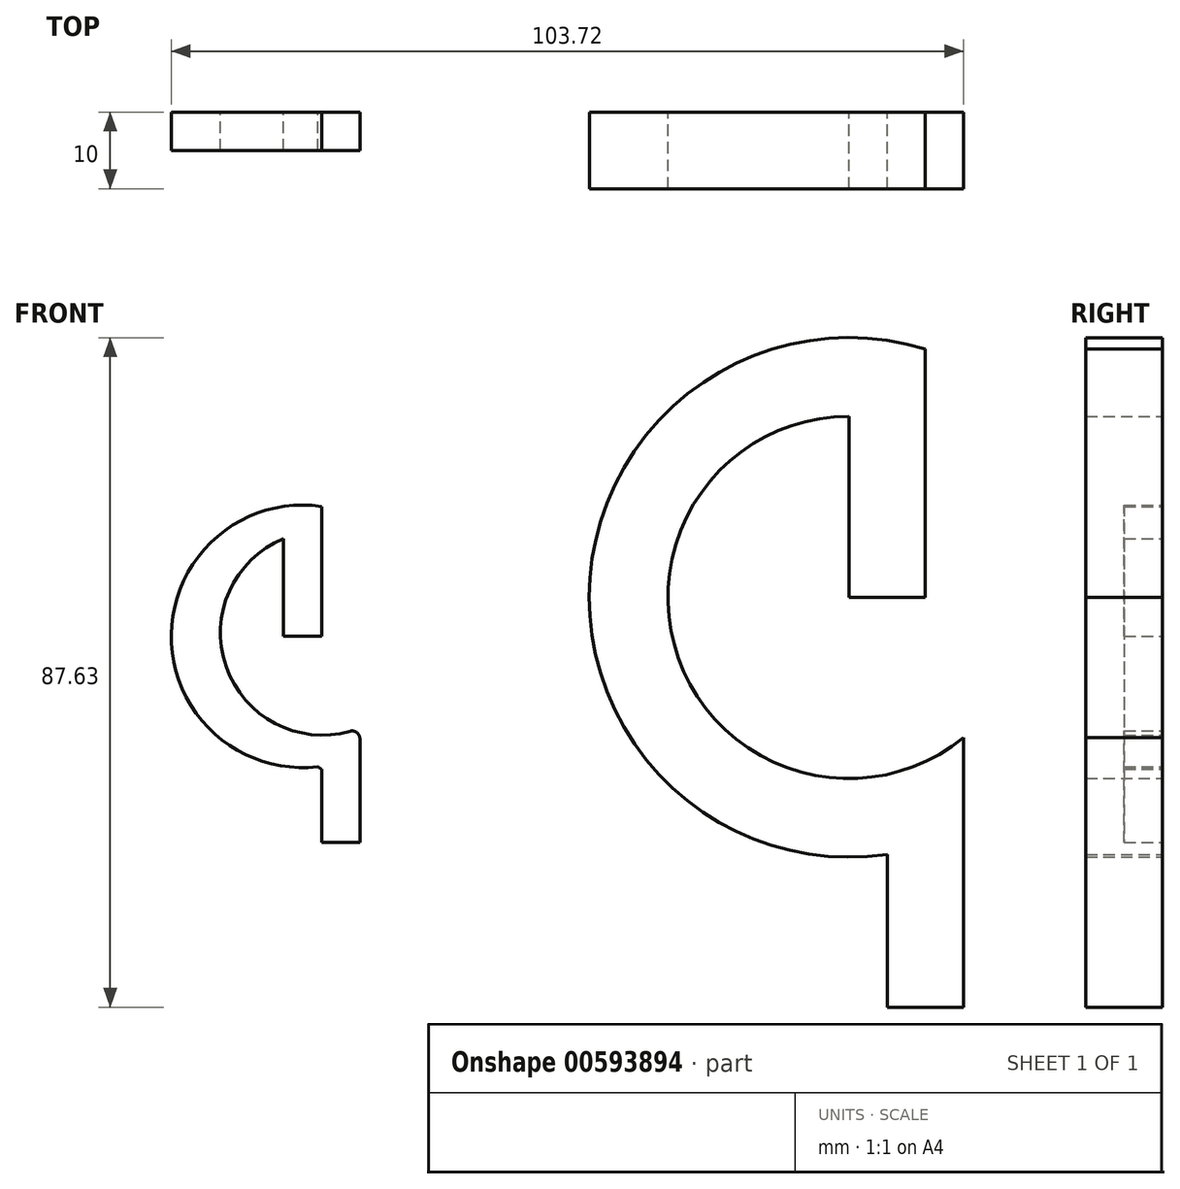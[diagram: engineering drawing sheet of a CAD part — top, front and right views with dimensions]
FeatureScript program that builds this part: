
annotation { "Feature Type Name" : "Feature", "Feature Type Description" : "" }
export const myFeature = defineFeature(function(context is Context, id is Id, definition is map)
    precondition{}
    {
        {
            var Q0;
            Q0=qCreatedBy(makeId("Front.planeOp"),FACE);
            var sketch = newSketch(context, id + "F0", { "sketchPlane" : qUnion([Q0])});
            skArc(sketch, "E0", {"start": v(-30.6, 46.04) * mm, "mid": v(-50.29, 29.04) * mm, "end": v(-30.6, 12.04) * mm});
            skLineSegment(sketch, "E1", {"start": v(-35.6, 41.83) * mm, "end": v(-35.6, 29.04) * mm});
            skLineSegment(sketch, "E2", {"start": v(-35.6, 29.04) * mm, "end": v(-30.6, 29.04) * mm});
            skLineSegment(sketch, "E3", {"start": v(-30.6, 29.04) * mm, "end": v(-30.6, 46.04) * mm});
            skPoint(sketch, "E4.orphan", {"position": v(-30.6, 26.78) * mm});
            skLineSegment(sketch, "E5", {"start": v(-30.6, 12.04) * mm, "end": v(-30.6, 2.04) * mm});
            skLineSegment(sketch, "E6", {"start": v(-30.6, 2.04) * mm, "end": v(-25.6, 2.04) * mm});
            skLineSegment(sketch, "E7", {"start": v(-25.6, 2.04) * mm, "end": v(-25.6, 15.65) * mm});
            skLineSegment(sketch, "E8", {"start": v(-35.6, 41.83) * mm, "end": v(-35.6, 31.04) * mm});
            skLineSegment(sketch, "E9", {"start": v(-35.6, 31.04) * mm, "end": v(-35.6, 41.83) * mm});
            skArc(sketch, "E10", {"start": v(-31.1, 11.97) * mm, "mid": v(-30.85, 11.8) * mm, "end": v(-30.6, 11.64) * mm});
            skPoint(sketch, "E11.orphan", {"position": v(-39.68, 41.83) * mm});
            skArc(sketch, "E12", {"start": v(-35.6, 41.83) * mm, "mid": v(-43.12, 25.1) * mm, "end": v(-26.88, 16.61) * mm});
            skPoint(sketch, "E13.visualSharp", {"position": v(-25.6, 17.04) * mm});
            skArc(sketch, "E13.filletArc", {"start": v(-25.6, 15.65) * mm, "mid": v(-26, 16.45) * mm, "end": v(-26.88, 16.61) * mm});
            skArc(sketch, "E14", {"start": v(48.43, 66.63) * mm, "mid": v(4.52, 36.7) * mm, "end": v(43.43, 0.5) * mm});
            skLineSegment(sketch, "E15", {"start": v(38.43, 34.13) * mm, "end": v(38.43, 58.13) * mm});
            skLineSegment(sketch, "E16", {"start": v(38.43, 34.13) * mm, "end": v(48.43, 34.13) * mm});
            skLineSegment(sketch, "E17", {"start": v(48.43, 34.13) * mm, "end": v(48.43, 66.63) * mm});
            skLineSegment(sketch, "E18", {"start": v(43.43, 0.5) * mm, "end": v(43.43, 0) * mm});
            skPoint(sketch, "E19.orphan", {"position": v(43.43, 34.13) * mm});
            skLineSegment(sketch, "E20", {"start": v(43.43, 0.5) * mm, "end": v(43.43, -19.5) * mm});
            skLineSegment(sketch, "E21", {"start": v(43.43, -19.5) * mm, "end": v(53.43, -19.5) * mm});
            skLineSegment(sketch, "E22", {"start": v(53.43, -19.5) * mm, "end": v(53.43, 10.5) * mm});
            skArc(sketch, "E23", {"start": v(38.43, 57.84) * mm, "mid": v(16.1, 26.17) * mm, "end": v(53.43, 15.78) * mm});
            skLineSegment(sketch, "E24", {"start": v(53.43, 10.5) * mm, "end": v(53.43, 15.78) * mm});
            skSolve(sketch);
        }
        {
            var Q0;
            Q0 = qSketchRegion(id + "F0", true);
            extrude(context, id + "F1", {"entities" : qUnion([Q0]), "depth" : 5 * mm, "offsetDistance" : 25 * mm});
        }
        {
            var Q0;
            Q0=makeQuery(id+"F1.opExtrude","CAP_FACE",FACE,{"disambiguationData":[OSD([sQuery(id+"F0.wireOp",EDGE,"E14"),sQuery(id+"F0.wireOp",EDGE,"E16"),sQuery(id+"F0.wireOp",EDGE,"E17"),sQuery(id+"F0.wireOp",EDGE,"E15"),sQuery(id+"F0.wireOp",EDGE,"E20"),sQuery(id+"F0.wireOp",EDGE,"E21"),sQuery(id+"F0.wireOp",EDGE,"E22"),sQuery(id+"F0.wireOp",EDGE,"E23"),sQuery(id+"F0.wireOp",EDGE,"E24")])],"isStart":false});
            extrude(context, id + "F2", {"entities" : qUnion([Q0]), "operationType" : NewBodyOperationType.ADD, "depth" : 5 * mm, "offsetDistance" : 25 * mm});
        }
    });
